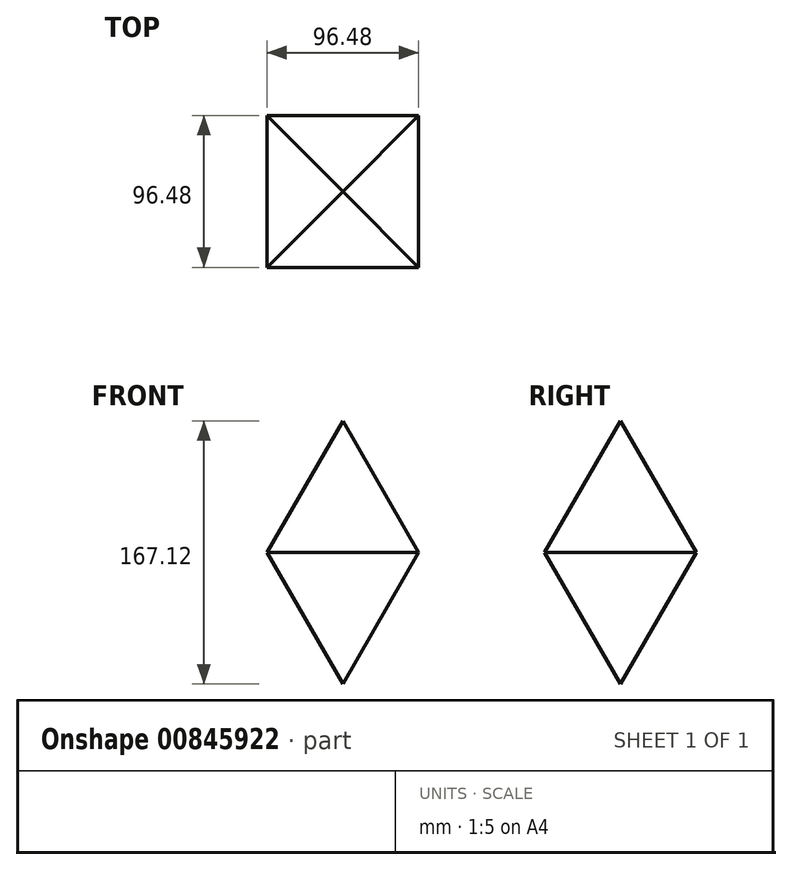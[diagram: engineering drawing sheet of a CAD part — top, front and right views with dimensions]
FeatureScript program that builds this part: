
annotation { "Feature Type Name" : "Feature", "Feature Type Description" : "" }
export const myFeature = defineFeature(function(context is Context, id is Id, definition is map)
    precondition{}
    {
        {
            var Q0;
            Q0=qCreatedBy(makeId("Top.planeOp"),FACE);
            var sketch = newSketch(context, id + "F0", { "sketchPlane" : qUnion([Q0])});
            skLineSegment(sketch, "E0.bottom", {"start": v(6.33, -30.37) * mm, "end": v(-90.15, -30.37) * mm});
            skLineSegment(sketch, "E0.top", {"start": v(6.33, 66.1) * mm, "end": v(-90.15, 66.1) * mm});
            skLineSegment(sketch, "E0.left", {"start": v(6.33, -30.37) * mm, "end": v(6.33, 66.1) * mm});
            skLineSegment(sketch, "E0.right", {"start": v(-90.15, -30.37) * mm, "end": v(-90.15, 66.1) * mm});
            skSolve(sketch);
        }
        {
            var Q0;
            Q0=makeQuery(id+"F0.imprint","IMPRINT",FACE,{"disambiguationData":[TD([[makeQuery(id+"F0.imprint","IMPRINT",EDGE,{"derivedFrom":sQuery(id+"F0.wireOp",EDGE,"E0.bottom")}),-1.0]])]});
            extrude(context, id + "F1", {"entities" : qUnion([Q0]), "depth" : 149.1 * mm, "offsetDistance" : 25.4 * mm, "hasDraft" : true, "draftAngle" : 30 * degree, "draftPullDirection" : true, "hasSecondDirection" : true, "secondDirectionOppositeDirection" : true, "secondDirectionDepth" : 116.33 * mm, "hasSecondDirectionDraft" : true, "secondDirectionDraftAngle" : 30 * degree, "secondDirectionDraftPullDirection" : true});
        }
    });
